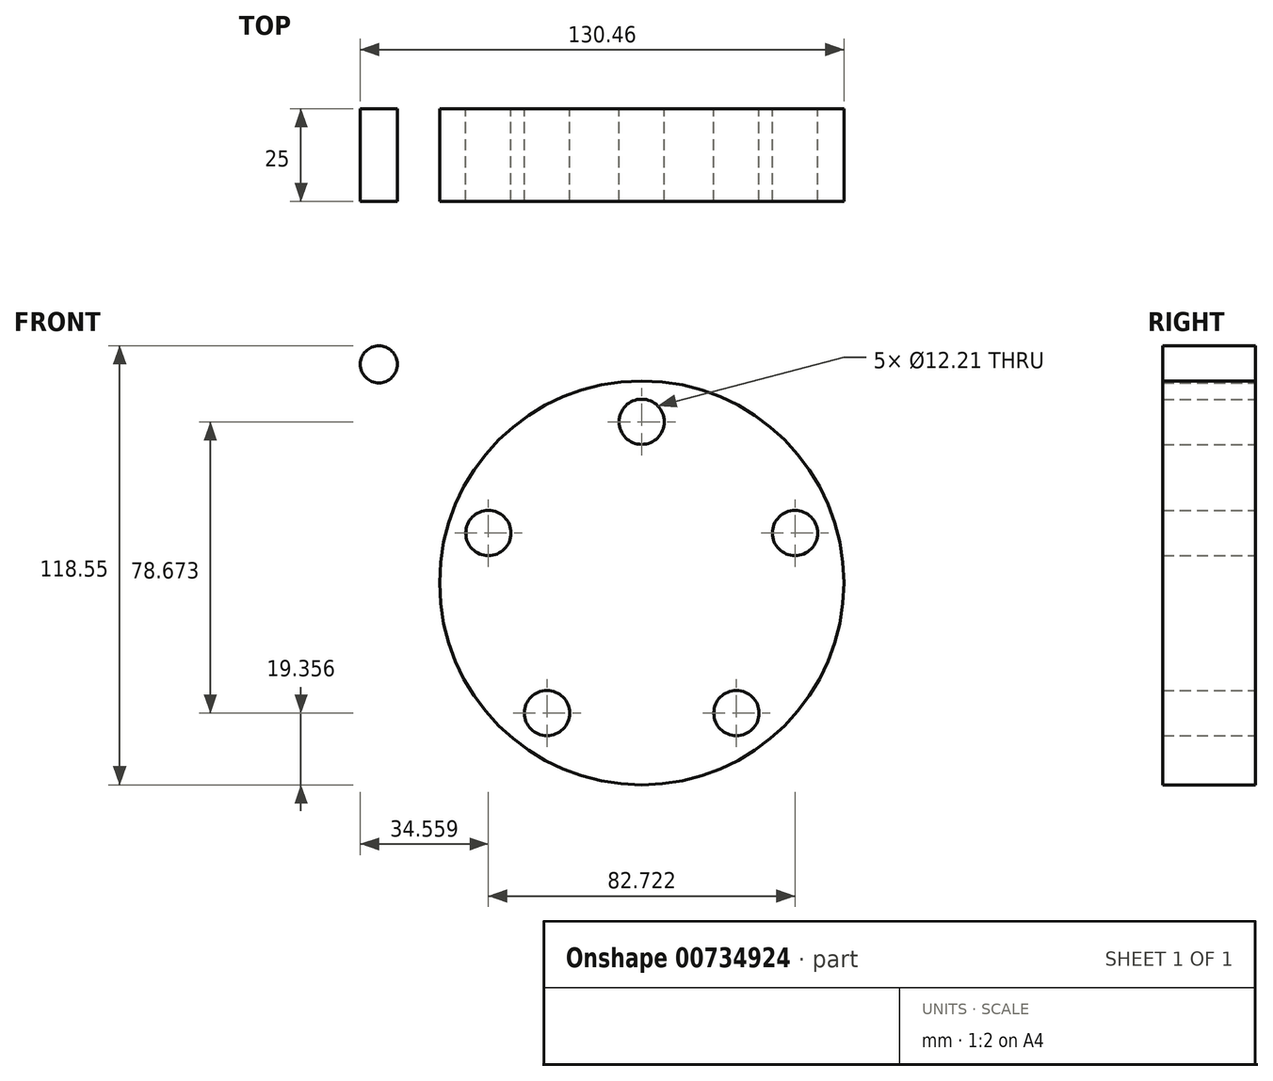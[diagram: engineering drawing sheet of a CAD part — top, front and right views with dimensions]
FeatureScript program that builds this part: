
annotation { "Feature Type Name" : "Feature", "Feature Type Description" : "" }
export const myFeature = defineFeature(function(context is Context, id is Id, definition is map)
    precondition{}
    {
        {
            var Q0;
            Q0=qCreatedBy(makeId("Front.planeOp"),FACE);
            var sketch = newSketch(context, id + "F0", { "sketchPlane" : qUnion([Q0])});
            skCircle(sketch, "E0", {"center": v(0, 0) * mm, "radius": 54.54 * mm});
            skCircle(sketch, "E1", {"center": v(0, 43.49) * mm, "radius": 6.1 * mm});
            skCircle(sketch, "E2.1.0", {"center": v(-41.36, 13.44) * mm, "radius": 6.1 * mm});
            skCircle(sketch, "E2.2.0", {"center": v(-25.56, -35.18) * mm, "radius": 6.1 * mm});
            skCircle(sketch, "E2.3.0", {"center": v(25.56, -35.18) * mm, "radius": 6.1 * mm});
            skCircle(sketch, "E2.4.0", {"center": v(41.36, 13.44) * mm, "radius": 6.1 * mm});
            skSolve(sketch);
        }
        {
            var Q0;
            Q0 = qSketchRegion(id + "F0", true);
            extrude(context, id + "F1", {"entities" : qUnion([Q0]), "depth" : 25 * mm, "offsetDistance" : 25 * mm});
        }
        {
            var Q0;
            Q0=qCreatedBy(makeId("Front.planeOp"),FACE);
            var sketch = newSketch(context, id + "F2", { "sketchPlane" : qUnion([Q0])});
            skCircle(sketch, "E3", {"center": v(-70.92, 59) * mm, "radius": 5 * mm});
            skSolve(sketch);
        }
        {
            var Q0;
            Q0 = qSketchRegion(id + "F2", true);
            extrude(context, id + "F3", {"entities" : qUnion([Q0]), "depth" : 25 * mm, "offsetDistance" : 25 * mm});
        }
    });
